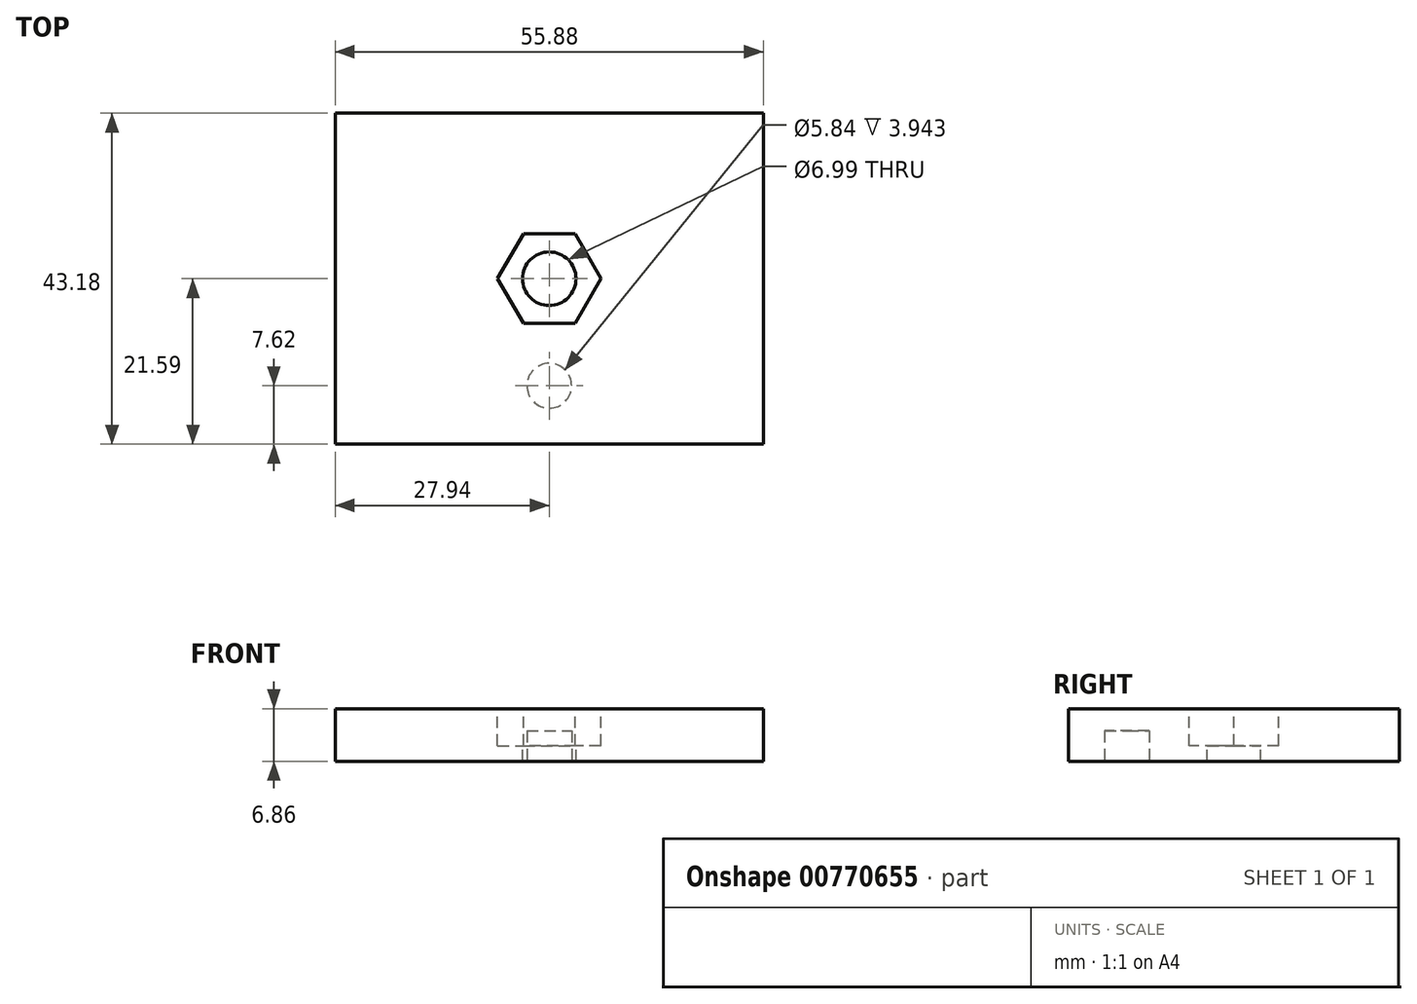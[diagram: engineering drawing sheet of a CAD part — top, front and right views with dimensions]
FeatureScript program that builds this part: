
annotation { "Feature Type Name" : "Feature", "Feature Type Description" : "" }
export const myFeature = defineFeature(function(context is Context, id is Id, definition is map)
    precondition{}
    {
        {
            var Q0;
            Q0=qCreatedBy(makeId("Top.planeOp"),FACE);
            var sketch = newSketch(context, id + "F0", { "sketchPlane" : qUnion([Q0])});
            skLineSegment(sketch, "E0", {"start": v(-27.94, 21.59) * mm, "end": v(-27.94, -21.59) * mm});
            skLineSegment(sketch, "E1", {"start": v(-27.94, -21.59) * mm, "end": v(27.94, -21.59) * mm});
            skLineSegment(sketch, "E2", {"start": v(27.94, -21.59) * mm, "end": v(27.94, 21.6) * mm});
            skLineSegment(sketch, "E3", {"start": v(27.94, 21.6) * mm, "end": v(-27.94, 21.59) * mm});
            skSolve(sketch);
        }
        {
            var Q0;
            Q0=makeQuery(id+"F0.imprint","IMPRINT",FACE,{"disambiguationData":[TD([[makeQuery(id+"F0.imprint","IMPRINT",EDGE,{"derivedFrom":sQuery(id+"F0.wireOp",EDGE,"E0")}),1.0]])]});
            extrude(context, id + "F1", {"entities" : qUnion([Q0]), "depth" : 6.86 * mm, "offsetDistance" : 25.4 * mm});
        }
        {
            var Q0;
            Q0=makeQuery(id+"F1.opExtrude","CAP_FACE",FACE,{"disambiguationData":[OSD([sQuery(id+"F0.wireOp",EDGE,"E0"),sQuery(id+"F0.wireOp",EDGE,"E1"),sQuery(id+"F0.wireOp",EDGE,"E2"),sQuery(id+"F0.wireOp",EDGE,"E3")])],"isStart":false});
            var sketch = newSketch(context, id + "F2", { "sketchPlane" : qUnion([Q0])});
            skCircle(sketch, "E4.cCircle", {"center": v(0, 0) * mm, "radius": 5.84 * mm, "construction": true});
            skLineSegment(sketch, "E4.0", {"start": v(6.75, 0) * mm, "end": v(3.37, -5.84) * mm});
            skLineSegment(sketch, "E4.1", {"start": v(3.37, -5.84) * mm, "end": v(-3.37, -5.84) * mm});
            skLineSegment(sketch, "E4.2", {"start": v(-3.37, -5.84) * mm, "end": v(-6.75, 0) * mm});
            skLineSegment(sketch, "E4.3", {"start": v(-6.75, 0) * mm, "end": v(-3.37, 5.84) * mm});
            skLineSegment(sketch, "E4.4", {"start": v(-3.37, 5.84) * mm, "end": v(3.37, 5.84) * mm});
            skLineSegment(sketch, "E4.5", {"start": v(3.37, 5.84) * mm, "end": v(6.75, 0) * mm});
            skPoint(sketch, "E4.0.midPoint", {"position": v(5.06, -2.92) * mm});
            skSolve(sketch);
        }
        {
            var Q0;
            Q0=makeQuery(id+"F1.opExtrude","CAP_FACE",FACE,{"disambiguationData":[OSD([sQuery(id+"F0.wireOp",EDGE,"E0"),sQuery(id+"F0.wireOp",EDGE,"E1"),sQuery(id+"F0.wireOp",EDGE,"E2"),sQuery(id+"F0.wireOp",EDGE,"E3")])],"isStart":true});
            var sketch = newSketch(context, id + "F3", { "sketchPlane" : qUnion([Q0])});
            skCircle(sketch, "E5", {"center": v(0, 13.97) * mm, "radius": 2.92 * mm});
            skSolve(sketch);
        }
        {
            var Q0;
            Q0=makeQuery(id+"F3.imprint","IMPRINT",FACE,{"disambiguationData":[TD([[makeQuery(id+"F3.imprint","IMPRINT",EDGE,{"derivedFrom":sQuery(id+"F3.wireOp",EDGE,"E5")}),1.0]])]});
            extrude(context, id + "F4", {"entities" : qUnion([Q0]), "operationType" : NewBodyOperationType.REMOVE, "oppositeDirection" : true, "depth" : 3.94 * mm, "offsetDistance" : 25.4 * mm});
        }
        {
            var Q0;
            Q0=makeQuery(id+"F2.imprint","IMPRINT",FACE,{"disambiguationData":[TD([[makeQuery(id+"F2.imprint","IMPRINT",EDGE,{"derivedFrom":sQuery(id+"F2.wireOp",EDGE,"E4.0")}),-1.0]])]});
            extrude(context, id + "F5", {"entities" : qUnion([Q0]), "operationType" : NewBodyOperationType.REMOVE, "oppositeDirection" : true, "depth" : 4.83 * mm, "offsetDistance" : 25.4 * mm});
        }
        {
            var Q0;
            Q0=makeQuery(id+"F5.boolean.opBoolean","COPY",FACE,{"derivedFrom":makeQuery(id+"F5.opExtrude","CAP_FACE",FACE,{"disambiguationData":[OSD([sQuery(id+"F2.wireOp",EDGE,"E4.0"),sQuery(id+"F2.wireOp",EDGE,"E4.1"),sQuery(id+"F2.wireOp",EDGE,"E4.2"),sQuery(id+"F2.wireOp",EDGE,"E4.3"),sQuery(id+"F2.wireOp",EDGE,"E4.4"),sQuery(id+"F2.wireOp",EDGE,"E4.5")])],"isStart":false})});
            var sketch = newSketch(context, id + "F6", { "sketchPlane" : qUnion([Q0])});
            skCircle(sketch, "E6", {"center": v(0, 0) * mm, "radius": 3.5 * mm});
            skSolve(sketch);
        }
        {
            var Q0;
            Q0=makeQuery(id+"F6.imprint","IMPRINT",FACE,{"disambiguationData":[TD([[makeQuery(id+"F6.imprint","IMPRINT",EDGE,{"derivedFrom":sQuery(id+"F6.wireOp",EDGE,"E6")}),1.0]])]});
            extrude(context, id + "F7", {"entities" : qUnion([Q0]), "operationType" : NewBodyOperationType.REMOVE, "oppositeDirection" : true, "depth" : 25.4 * mm, "offsetDistance" : 25.4 * mm});
        }
    });
